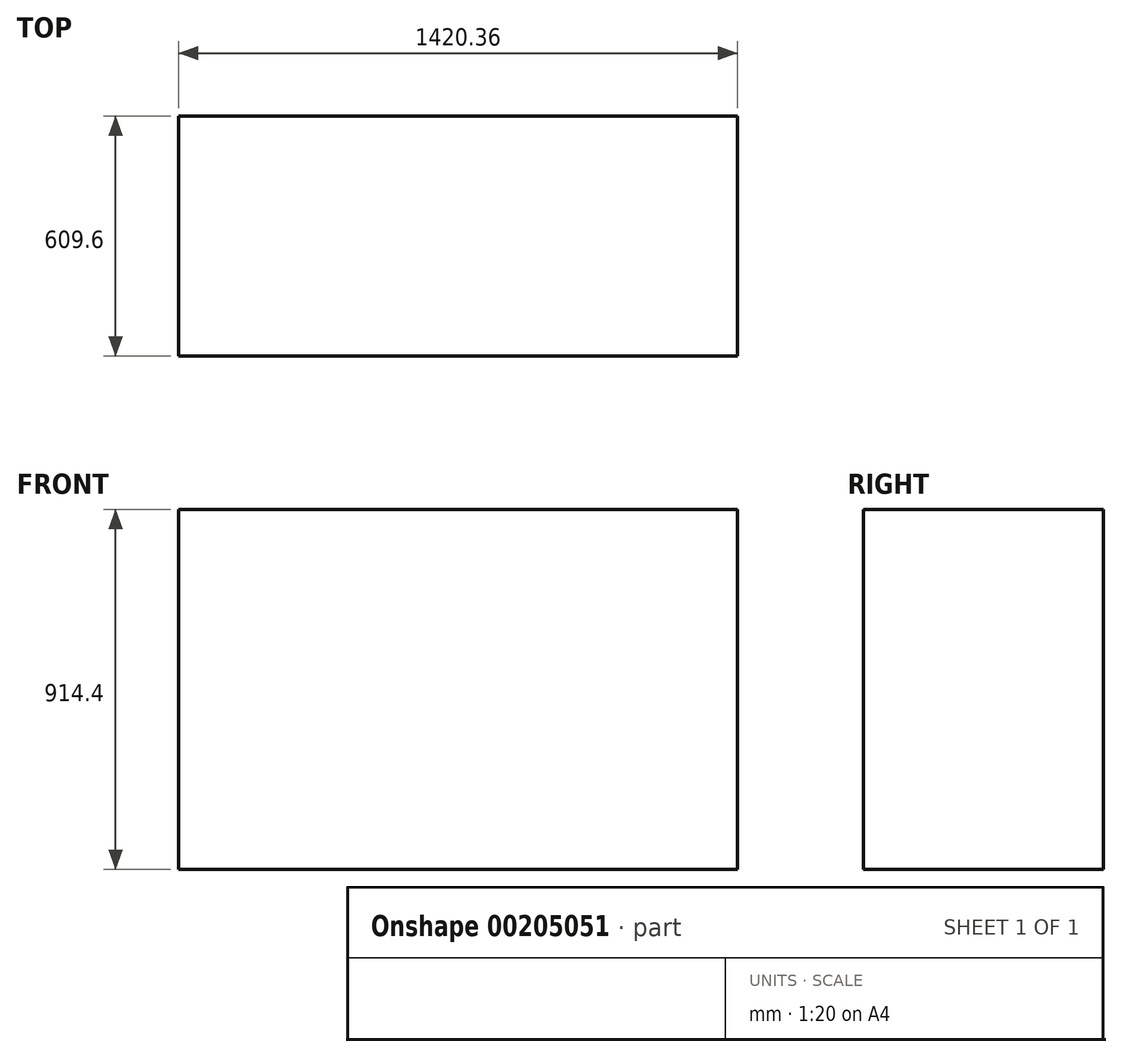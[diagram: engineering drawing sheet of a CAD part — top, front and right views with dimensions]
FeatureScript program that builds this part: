
annotation { "Feature Type Name" : "Feature", "Feature Type Description" : "" }
export const myFeature = defineFeature(function(context is Context, id is Id, definition is map)
    precondition{}
    {
        {
            var Q0;
            Q0=qCreatedBy(makeId("Top.planeOp"),FACE);
            var sketch = newSketch(context, id + "F0", { "sketchPlane" : qUnion([Q0])});
            skLineSegment(sketch, "E0.bottom", {"start": v(710.18, 304.8) * mm, "end": v(-710.18, 304.8) * mm});
            skLineSegment(sketch, "E0.top", {"start": v(710.18, -304.8) * mm, "end": v(-710.18, -304.8) * mm});
            skLineSegment(sketch, "E0.left", {"start": v(710.18, 304.8) * mm, "end": v(710.18, -304.8) * mm});
            skLineSegment(sketch, "E0.right", {"start": v(-710.18, 304.8) * mm, "end": v(-710.18, -304.8) * mm});
            skPoint(sketch, "E0.middle", {"position": v(0, 0) * mm});
            skSolve(sketch);
        }
        {
            var Q0;
            Q0 = qSketchRegion(id + "F0", true);
            extrude(context, id + "F1", {"entities" : qUnion([Q0]), "depth" : 914.4 * mm});
        }
    });
